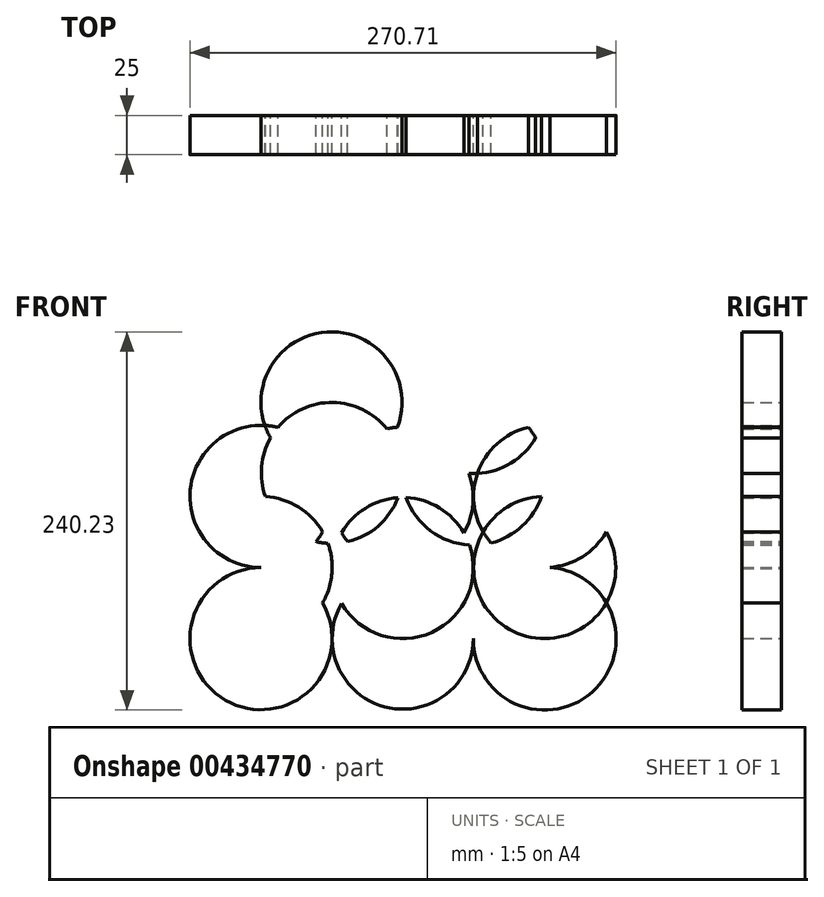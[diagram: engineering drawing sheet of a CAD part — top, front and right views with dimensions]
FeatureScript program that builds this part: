
annotation { "Feature Type Name" : "Feature", "Feature Type Description" : "" }
export const myFeature = defineFeature(function(context is Context, id is Id, definition is map)
    precondition{}
    {
        {
            var Q0;
            Q0=qCreatedBy(makeId("Front.planeOp"),FACE);
            var sketch = newSketch(context, id + "F0", { "sketchPlane" : qUnion([Q0])});
            skCircle(sketch, "E0", {"center": v(0, 0) * mm, "radius": 44.8 * mm});
            skCircle(sketch, "E1", {"center": v(-89.97, 0) * mm, "radius": 45.16 * mm});
            skCircle(sketch, "E2", {"center": v(90.2, 0) * mm, "radius": 45.39 * mm});
            skCircle(sketch, "E3", {"center": v(-89.96, 45.16) * mm, "radius": 45.16 * mm});
            skCircle(sketch, "E4", {"center": v(0, 44.8) * mm, "radius": 44.8 * mm});
            skCircle(sketch, "E5", {"center": v(90.2, 45.16) * mm, "radius": 45.16 * mm});
            skCircle(sketch, "E6", {"center": v(-89.96, 90.32) * mm, "radius": 45.16 * mm});
            skCircle(sketch, "E7", {"center": v(0, 89.61) * mm, "radius": 44.8 * mm});
            skCircle(sketch, "E8", {"center": v(90.2, 90.32) * mm, "radius": 45.16 * mm});
            skCircle(sketch, "E9", {"center": v(-45.21, 150.04) * mm, "radius": 44.8 * mm});
            skCircle(sketch, "E10", {"center": v(45.08, 150.4) * mm, "radius": 45.5 * mm});
            skCircle(sketch, "E11", {"center": v(-45.02, 105.25) * mm, "radius": 44.8 * mm});
            skCircle(sketch, "E12", {"center": v(45, 104.9) * mm, "radius": 45.5 * mm});
            skSolve(sketch);
        }
        {
            var Q0;
            {var subQ0=sQuery(id+"F0.wireOp",EDGE,"E9");var subQ1=sQuery(id+"F0.wireOp",EDGE,"E6");var subQ2=makeQuery(id+"F0.imprint","INTERSECT",VERTEX,{"disambiguationData":[OD(0.0)],"derivedFrom":[subQ1,subQ0]});Q0=makeQuery(id+"F0.imprint","IMPRINT",FACE,{"disambiguationData":[TD([[makeQuery(id+"F0.imprint","IMPRINT",EDGE,{"disambiguationData":[TD([[subQ2,1.0]])],"derivedFrom":subQ1}),-1.0]])]});}
            var Q1;
            {var subQ0=sQuery(id+"F0.wireOp",EDGE,"E11");var subQ1=sQuery(id+"F0.wireOp",EDGE,"E6");var subQ2=makeQuery(id+"F0.imprint","INTERSECT",VERTEX,{"disambiguationData":[OD(0.0)],"derivedFrom":[subQ1,subQ0]});Q1=makeQuery(id+"F0.imprint","IMPRINT",FACE,{"disambiguationData":[TD([[makeQuery(id+"F0.imprint","IMPRINT",EDGE,{"disambiguationData":[TD([[subQ2,1.0]])],"derivedFrom":subQ1}),1.0]])]});}
            var Q2;
            {var subQ0=sQuery(id+"F0.wireOp",EDGE,"E6");var subQ1=sQuery(id+"F0.wireOp",EDGE,"E3");var subQ2=makeQuery(id+"F0.imprint","INTERSECT",VERTEX,{"disambiguationData":[OD(1.0)],"derivedFrom":[subQ1,subQ0]});Q2=makeQuery(id+"F0.imprint","IMPRINT",FACE,{"disambiguationData":[TD([[makeQuery(id+"F0.imprint","IMPRINT",EDGE,{"disambiguationData":[TD([[subQ2,-1.0]])],"derivedFrom":subQ1}),1.0]])]});}
            var Q3;
            {var subQ0=sQuery(id+"F0.wireOp",EDGE,"E11");var subQ1=sQuery(id+"F0.wireOp",EDGE,"E4");var subQ2=makeQuery(id+"F0.imprint","INTERSECT",VERTEX,{"disambiguationData":[OD(0.0)],"derivedFrom":[subQ1,subQ0]});Q3=makeQuery(id+"F0.imprint","IMPRINT",FACE,{"disambiguationData":[TD([[makeQuery(id+"F0.imprint","IMPRINT",EDGE,{"disambiguationData":[TD([[subQ2,-1.0]])],"derivedFrom":subQ1}),1.0]])]});}
            var Q4;
            {var subQ0=sQuery(id+"F0.wireOp",EDGE,"E7");var subQ1=sQuery(id+"F0.wireOp",EDGE,"E4");var subQ2=makeQuery(id+"F0.imprint","INTERSECT",VERTEX,{"disambiguationData":[OD(0.0)],"derivedFrom":[subQ1,subQ0]});Q4=makeQuery(id+"F0.imprint","IMPRINT",FACE,{"disambiguationData":[TD([[makeQuery(id+"F0.imprint","IMPRINT",EDGE,{"disambiguationData":[TD([[subQ2,-1.0]])],"derivedFrom":subQ1}),1.0]])]});}
            var Q5;
            {var subQ0=sQuery(id+"F0.wireOp",EDGE,"E12");var subQ1=sQuery(id+"F0.wireOp",EDGE,"E8");var subQ2=makeQuery(id+"F0.imprint","INTERSECT",VERTEX,{"disambiguationData":[OD(0.0)],"derivedFrom":[subQ1,subQ0]});Q5=makeQuery(id+"F0.imprint","IMPRINT",FACE,{"disambiguationData":[TD([[makeQuery(id+"F0.imprint","IMPRINT",EDGE,{"disambiguationData":[TD([[subQ2,-1.0]])],"derivedFrom":subQ1}),1.0]])]});}
            var Q6;
            {var subQ0=sQuery(id+"F0.wireOp",EDGE,"E12");var subQ1=sQuery(id+"F0.wireOp",EDGE,"E5");var subQ2=makeQuery(id+"F0.imprint","INTERSECT",VERTEX,{"disambiguationData":[OD(0.0)],"derivedFrom":[subQ1,subQ0]});Q6=makeQuery(id+"F0.imprint","IMPRINT",FACE,{"disambiguationData":[TD([[makeQuery(id+"F0.imprint","IMPRINT",EDGE,{"disambiguationData":[TD([[subQ2,-1.0]])],"derivedFrom":subQ1}),1.0]])]});}
            var Q7;
            {var subQ1=sQuery(id+"F0.wireOp",EDGE,"E3");var subQ4=sQuery(id+"F0.wireOp",EDGE,"E1");var subQ5=makeQuery(id+"F0.imprint","INTERSECT",VERTEX,{"disambiguationData":[OD(1.0)],"derivedFrom":[subQ4,subQ1]});Q7=makeQuery(id+"F0.imprint","IMPRINT",FACE,{"disambiguationData":[TD([[makeQuery(id+"F0.imprint","IMPRINT",EDGE,{"disambiguationData":[TD([[subQ5,-1.0]])],"derivedFrom":subQ4}),-1.0]])]});}
            var Q8;
            {var subQ0=sQuery(id+"F0.wireOp",EDGE,"E5");var subQ1=sQuery(id+"F0.wireOp",EDGE,"E2");var subQ2=makeQuery(id+"F0.imprint","INTERSECT",VERTEX,{"disambiguationData":[OD(0.0)],"derivedFrom":[subQ1,subQ0]});Q8=makeQuery(id+"F0.imprint","IMPRINT",FACE,{"disambiguationData":[TD([[makeQuery(id+"F0.imprint","IMPRINT",EDGE,{"disambiguationData":[TD([[subQ2,-1.0]])],"derivedFrom":subQ1}),-1.0]])]});}
            var Q9;
            {var subQ0=sQuery(id+"F0.wireOp",EDGE,"E7");var subQ1=sQuery(id+"F0.wireOp",EDGE,"E4");var subQ2=makeQuery(id+"F0.imprint","INTERSECT",VERTEX,{"disambiguationData":[OD(0.0)],"derivedFrom":[subQ1,subQ0]});Q9=makeQuery(id+"F0.imprint","IMPRINT",FACE,{"disambiguationData":[TD([[makeQuery(id+"F0.imprint","IMPRINT",EDGE,{"disambiguationData":[TD([[subQ2,1.0]])],"derivedFrom":subQ1}),-1.0]])]});}
            var Q10;
            {var subQ1=sQuery(id+"F0.wireOp",EDGE,"E0");var subQ5=sQuery(id+"F0.wireOp",EDGE,"E2");var subQ6=makeQuery(id+"F0.imprint","INTERSECT",VERTEX,{"derivedFrom":[subQ1,subQ5]});Q10=makeQuery(id+"F0.imprint","IMPRINT",FACE,{"disambiguationData":[TD([[makeQuery(id+"F0.imprint","IMPRINT",EDGE,{"disambiguationData":[TD([[subQ6,-1.0]])],"derivedFrom":subQ1}),-1.0]])]});}
            var Q11;
            {var subQ0=sQuery(id+"F0.wireOp",EDGE,"E0");var subQ1=makeQuery(id+"F0.imprint","INTERSECT",VERTEX,{"derivedFrom":[subQ0,sQuery(id+"F0.wireOp",EDGE,"E2")]});Q11=makeQuery(id+"F0.imprint","IMPRINT",FACE,{"disambiguationData":[TD([[makeQuery(id+"F0.imprint","IMPRINT",EDGE,{"disambiguationData":[TD([[subQ1,-1.0]])],"derivedFrom":subQ0}),1.0]])]});}
            var Q12;
            {var subQ0=sQuery(id+"F0.wireOp",EDGE,"E2");var subQ1=makeQuery(id+"F0.imprint","INTERSECT",VERTEX,{"derivedFrom":[sQuery(id+"F0.wireOp",EDGE,"E0"),subQ0]});Q12=makeQuery(id+"F0.imprint","IMPRINT",FACE,{"disambiguationData":[TD([[makeQuery(id+"F0.imprint","IMPRINT",EDGE,{"disambiguationData":[TD([[subQ1,1.0]])],"derivedFrom":subQ0}),1.0]])]});}
            var Q13;
            {var subQ4=sQuery(id+"F0.wireOp",EDGE,"E12");var subQ5=sQuery(id+"F0.wireOp",EDGE,"E7");var subQ6=makeQuery(id+"F0.imprint","INTERSECT",VERTEX,{"disambiguationData":[OD(0.0)],"derivedFrom":[subQ5,subQ4]});Q13=makeQuery(id+"F0.imprint","IMPRINT",FACE,{"disambiguationData":[TD([[makeQuery(id+"F0.imprint","IMPRINT",EDGE,{"disambiguationData":[TD([[subQ6,-1.0]])],"derivedFrom":subQ5}),-1.0]])]});}
            var Q14;
            {var subQ0=sQuery(id+"F0.wireOp",EDGE,"E3");var subQ1=sQuery(id+"F0.wireOp",EDGE,"E1");var subQ2=makeQuery(id+"F0.imprint","INTERSECT",VERTEX,{"disambiguationData":[OD(1.0)],"derivedFrom":[subQ1,subQ0]});Q14=makeQuery(id+"F0.imprint","IMPRINT",FACE,{"disambiguationData":[TD([[makeQuery(id+"F0.imprint","IMPRINT",EDGE,{"disambiguationData":[TD([[subQ2,-1.0]])],"derivedFrom":subQ1}),1.0]])]});}
            var Q15;
            {var subQ0=sQuery(id+"F0.wireOp",EDGE,"E1");var subQ1=makeQuery(id+"F0.imprint","INTERSECT",VERTEX,{"derivedFrom":[sQuery(id+"F0.wireOp",EDGE,"E0"),subQ0]});Q15=makeQuery(id+"F0.imprint","IMPRINT",FACE,{"disambiguationData":[TD([[makeQuery(id+"F0.imprint","IMPRINT",EDGE,{"disambiguationData":[TD([[subQ1,-1.0]])],"derivedFrom":subQ0}),1.0]])]});}
            var Q16;
            {var subQ0=sQuery(id+"F0.wireOp",EDGE,"E6");var subQ1=sQuery(id+"F0.wireOp",EDGE,"E3");var subQ2=makeQuery(id+"F0.imprint","INTERSECT",VERTEX,{"disambiguationData":[OD(0.0)],"derivedFrom":[subQ1,subQ0]});Q16=makeQuery(id+"F0.imprint","IMPRINT",FACE,{"disambiguationData":[TD([[makeQuery(id+"F0.imprint","IMPRINT",EDGE,{"disambiguationData":[TD([[subQ2,1.0]])],"derivedFrom":subQ1}),-1.0]])]});}
            extrude(context, id + "F1", {"entities" : qUnion([Q0, Q1, Q2, Q3, Q4, Q5, Q6, Q7, Q8, Q9, Q10, Q11, Q12, Q13, Q14, Q15, Q16]), "depth" : 25 * mm});
        }
    });
